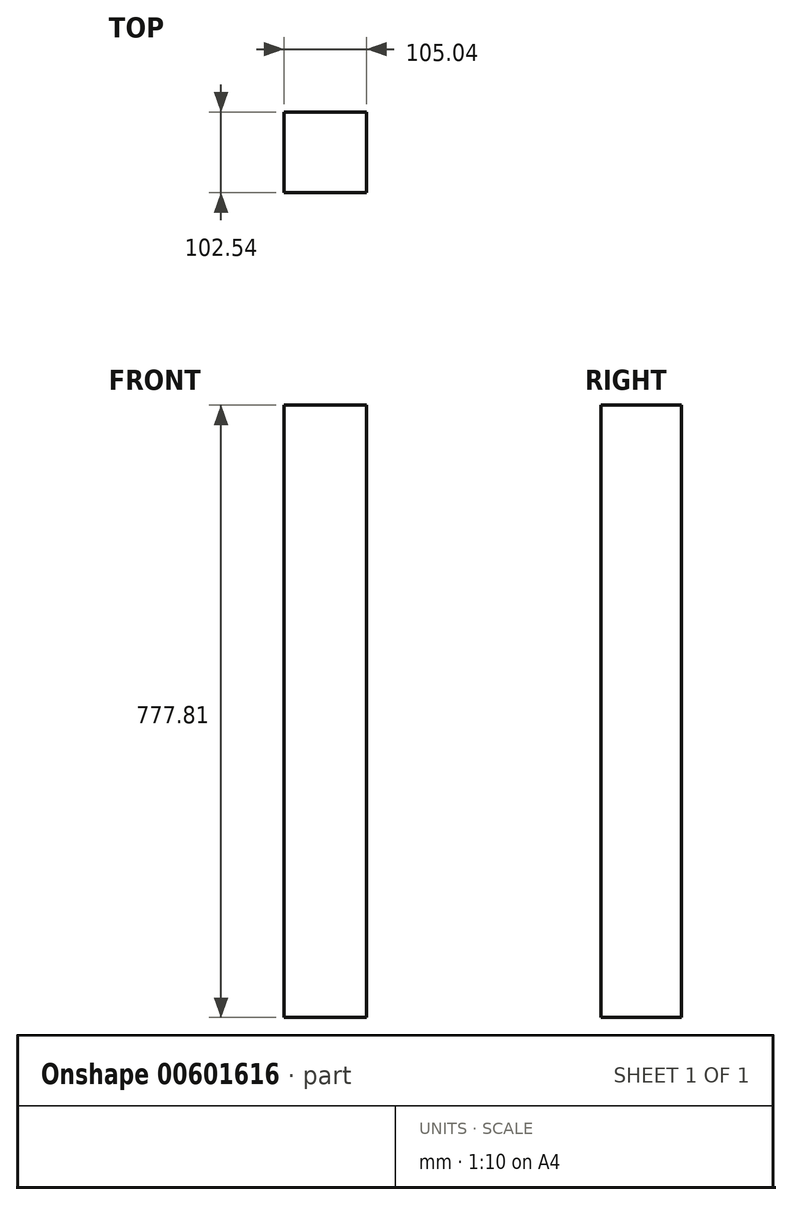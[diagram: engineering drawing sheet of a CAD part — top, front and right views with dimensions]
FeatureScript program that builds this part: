
annotation { "Feature Type Name" : "Feature", "Feature Type Description" : "" }
export const myFeature = defineFeature(function(context is Context, id is Id, definition is map)
    precondition{}
    {
        {
            var Q0;
            Q0=qCreatedBy(makeId("Top.planeOp"),FACE);
            var sketch = newSketch(context, id + "F0", { "sketchPlane" : qUnion([Q0])});
            skLineSegment(sketch, "E0.bottom", {"start": v(52.52, -51.27) * mm, "end": v(-52.52, -51.27) * mm});
            skLineSegment(sketch, "E0.top", {"start": v(52.52, 51.27) * mm, "end": v(-52.52, 51.27) * mm});
            skLineSegment(sketch, "E0.left", {"start": v(52.52, -51.27) * mm, "end": v(52.52, 51.27) * mm});
            skLineSegment(sketch, "E0.right", {"start": v(-52.52, -51.27) * mm, "end": v(-52.52, 51.27) * mm});
            skPoint(sketch, "E0.middle", {"position": v(0, 0) * mm});
            skSolve(sketch);
        }
        {
            var Q0;
            Q0=makeQuery(id+"F0.imprint","IMPRINT",FACE,{"disambiguationData":[TD([[makeQuery(id+"F0.imprint","IMPRINT",EDGE,{"derivedFrom":sQuery(id+"F0.wireOp",EDGE,"E0.bottom")}),-1.0]])]});
            extrude(context, id + "F1", {"entities" : qUnion([Q0]), "depth" : 777.8 * mm, "offsetDistance" : 25.4 * mm});
        }
    });
